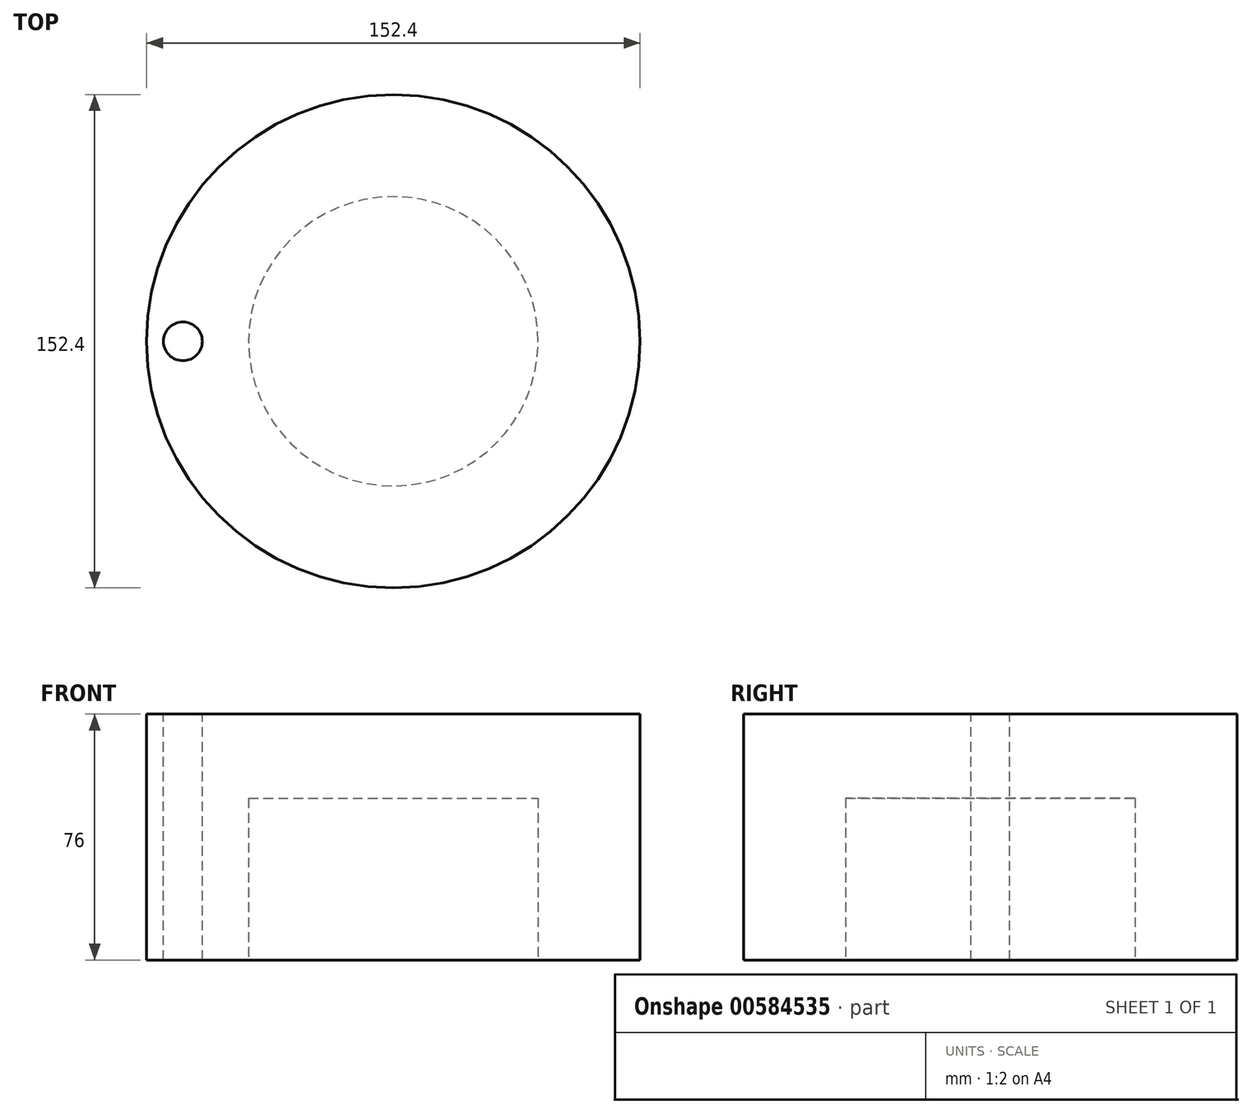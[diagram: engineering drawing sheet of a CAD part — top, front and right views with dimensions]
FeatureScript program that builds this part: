
annotation { "Feature Type Name" : "Feature", "Feature Type Description" : "" }
export const myFeature = defineFeature(function(context is Context, id is Id, definition is map)
    precondition{}
    {
        {
            var Q0;
            Q0=qCreatedBy(makeId("Top.planeOp"),FACE);
            var sketch = newSketch(context, id + "F0", { "sketchPlane" : qUnion([Q0])});
            skCircle(sketch, "E0", {"center": v(0, 0) * mm, "radius": 76.2 * mm});
            skSolve(sketch);
        }
        {
            var Q0;
            Q0=makeQuery(id+"F0.imprint","IMPRINT",FACE,{"disambiguationData":[TD([[makeQuery(id+"F0.imprint","IMPRINT",EDGE,{"derivedFrom":sQuery(id+"F0.wireOp",EDGE,"E0")}),1.0]])]});
            extrude(context, id + "F1", {"entities" : qUnion([Q0]), "depth" : 76 * mm, "offsetDistance" : 25 * mm});
        }
        {
            var Q0;
            Q0=makeQuery(id+"F1.opExtrude","CAP_FACE",FACE,{"disambiguationData":[OSD([sQuery(id+"F0.wireOp",EDGE,"E0")])],"isStart":true});
            var sketch = newSketch(context, id + "F2", { "sketchPlane" : qUnion([Q0])});
            skCircle(sketch, "E1", {"center": v(0, 0) * mm, "radius": 44.7 * mm});
            skSolve(sketch);
        }
        {
            var Q0;
            Q0=makeQuery(id+"F2.imprint","IMPRINT",FACE,{"disambiguationData":[TD([[makeQuery(id+"F2.imprint","IMPRINT",EDGE,{"derivedFrom":sQuery(id+"F2.wireOp",EDGE,"E1")}),1.0]])]});
            extrude(context, id + "F3", {"entities" : qUnion([Q0]), "operationType" : NewBodyOperationType.REMOVE, "oppositeDirection" : true, "depth" : 50 * mm, "offsetDistance" : 25 * mm});
        }
        {
            var Q0;
            Q0=makeQuery(id+"F1.opExtrude","CAP_FACE",FACE,{"disambiguationData":[OSD([sQuery(id+"F0.wireOp",EDGE,"E0")])],"isStart":false});
            var sketch = newSketch(context, id + "F4", { "sketchPlane" : qUnion([Q0])});
            skCircle(sketch, "E2", {"center": v(-65, 0) * mm, "radius": 6 * mm});
            skSolve(sketch);
        }
        {
            var Q0;
            Q0=makeQuery(id+"F4.imprint","IMPRINT",FACE,{"disambiguationData":[TD([[makeQuery(id+"F4.imprint","IMPRINT",EDGE,{"derivedFrom":sQuery(id+"F4.wireOp",EDGE,"E2")}),1.0]])]});
            extrude(context, id + "F5", {"entities" : qUnion([Q0]), "operationType" : NewBodyOperationType.REMOVE, "oppositeDirection" : true, "depth" : 76 * mm, "offsetDistance" : 25 * mm});
        }
    });
